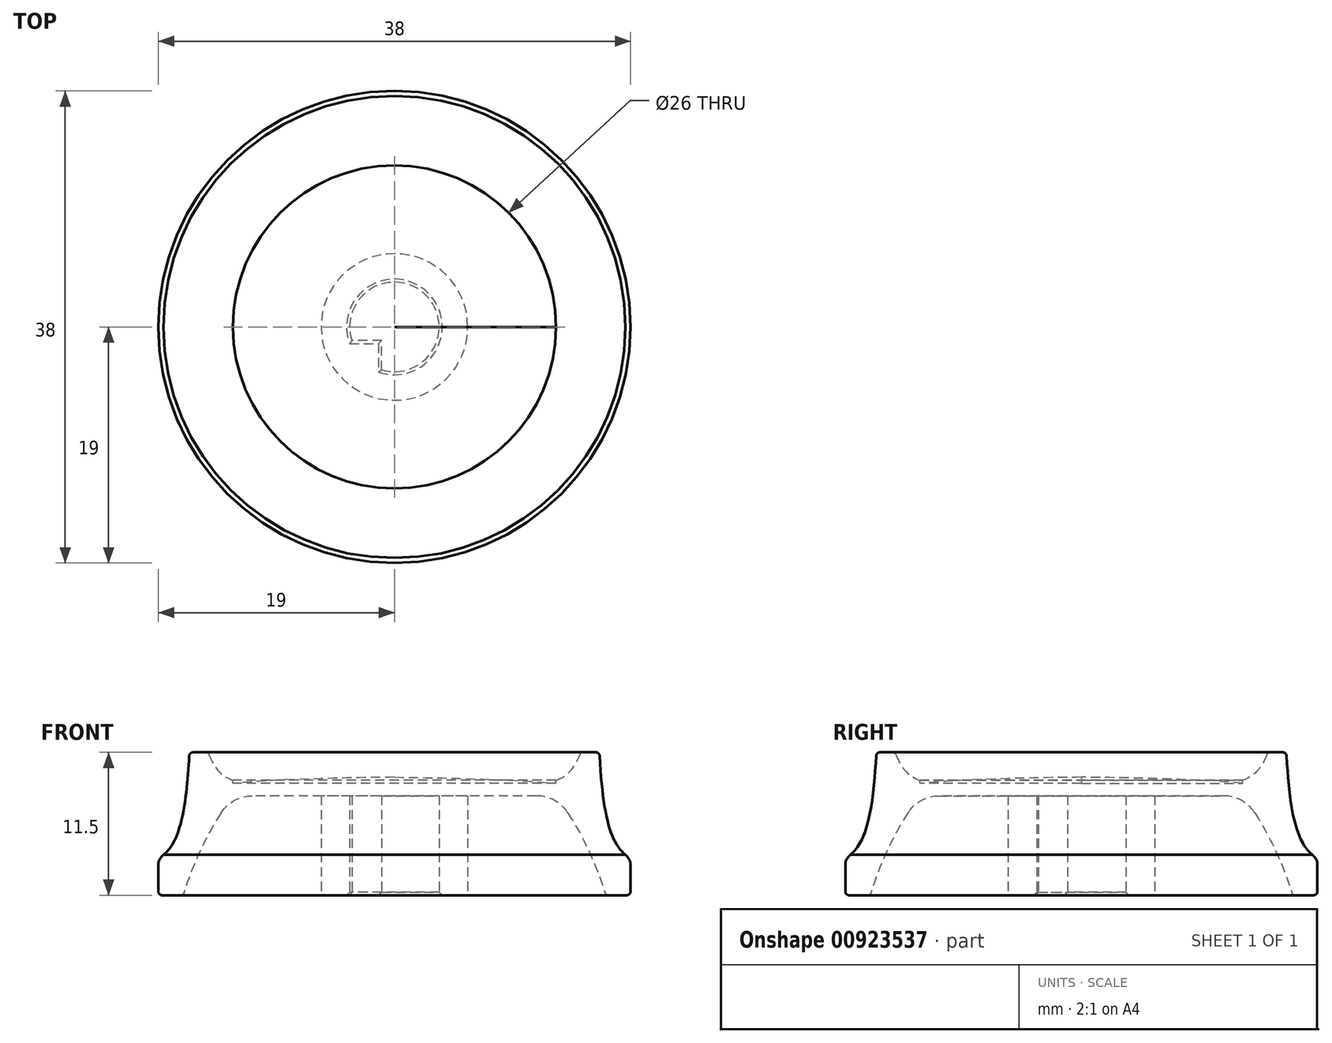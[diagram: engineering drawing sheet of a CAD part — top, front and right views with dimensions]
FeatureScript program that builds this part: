
annotation { "Feature Type Name" : "Feature", "Feature Type Description" : "" }
export const myFeature = defineFeature(function(context is Context, id is Id, definition is map)
    precondition{}
    {
        {
            var Q0;
            Q0=qCreatedBy(makeId("Top.planeOp"),FACE);
            var sketch = newSketch(context, id + "F0", { "sketchPlane" : qUnion([Q0])});
            skCircle(sketch, "E0", {"center": v(0, 0) * mm, "radius": 3.6 * mm});
            skLineSegment(sketch, "E1", {"start": v(0, -3.6) * mm, "end": v(0, -1.1) * mm});
            skLineSegment(sketch, "E2", {"start": v(0, -1.1) * mm, "end": v(3.43, -1.1) * mm});
            skLineSegment(sketch, "E3", {"start": v(3.43, -1.1) * mm, "end": v(1.03, -1.1) * mm});
            skLineSegment(sketch, "E4", {"start": v(1.03, -1.1) * mm, "end": v(1.03, -3.45) * mm});
            skLineSegment(sketch, "E5.MirrorCS", {"start": v(-1.03, -1.1) * mm, "end": v(-1.03, -3.45) * mm});
            skLineSegment(sketch, "E6.MirrorCS", {"start": v(0, -1.1) * mm, "end": v(-3.43, -1.1) * mm});
            skCircle(sketch, "E7.0", {"center": v(0, 0) * mm, "radius": 5.9 * mm});
            skCircle(sketch, "E8.0", {"center": v(0, 0) * mm, "radius": 5.1 * mm});
            skCircle(sketch, "E9.0", {"center": v(0, 0) * mm, "radius": 4.9 * mm});
            skSolve(sketch);
        }
        {
            var Q0;
            Q0 = qSketchRegion(id + "F0", true);
            var Q1;
            {var subQ0=sQuery(id+"F0.wireOp",EDGE,"E5.MirrorCS");Q1=makeQuery(id+"F0.imprint","IMPRINT",FACE,{"disambiguationData":[TD([[makeQuery(id+"F0.imprint","IMPRINT",EDGE,{"derivedFrom":subQ0}),-1.0]])]});}
            var Q2;
            {var subQ0=sQuery(id+"F0.wireOp",EDGE,"E3");Q2=makeQuery(id+"F0.imprint","IMPRINT",FACE,{"disambiguationData":[TD([[makeQuery(id+"F0.imprint","IMPRINT",EDGE,{"derivedFrom":subQ0}),1.0]])]});}
            var Q3;
            Q3=makeQuery(id+"F0.imprint","IMPRINT",FACE,{"disambiguationData":[TD([[makeQuery(id+"F0.imprint","IMPRINT",EDGE,{"derivedFrom":sQuery(id+"F0.wireOp",EDGE,"E9.0")}),1.0]])]});
            var Q4;
            Q4=makeQuery(id+"F0.imprint","IMPRINT",FACE,{"disambiguationData":[TD([[makeQuery(id+"F0.imprint","IMPRINT",EDGE,{"derivedFrom":sQuery(id+"F0.wireOp",EDGE,"E8.0")}),1.0]])]});
            extrude(context, id + "F1", {"entities" : qUnion([Q0, Q1, Q2, Q3, Q4]), "depth" : 8 * mm, "offsetDistance" : 25 * mm});
        }
        {
            var Q0;
            Q0=makeQuery(id+"F1.opExtrude","CAP_FACE",FACE,{"disambiguationData":[OSD([sQuery(id+"F0.wireOp",EDGE,"E0"),sQuery(id+"F0.wireOp",EDGE,"E3"),sQuery(id+"F0.wireOp",EDGE,"E4"),sQuery(id+"F0.wireOp",EDGE,"E5.MirrorCS"),sQuery(id+"F0.wireOp",EDGE,"E6.MirrorCS"),sQuery(id+"F0.wireOp",EDGE,"E7.0")])],"isStart":false});
            cPlane(context, id + "F2", {"entities" : qUnion([Q0]), "cplaneType" : CPlaneType.OFFSET, "offset" : 0 * mm, "width" : 150 * mm, "height" : 150 * mm});
        }
        {
            var Q0;
            Q0=qCreatedBy(id+"F2.planeOp",FACE);
            var sketch = newSketch(context, id + "F3", { "sketchPlane" : qUnion([Q0])});
            skCircle(sketch, "E10", {"center": v(0, 0) * mm, "radius": 5.9 * mm});
            skCircle(sketch, "E11.0", {"center": v(0, 0) * mm, "radius": 13 * mm});
            skSolve(sketch);
        }
        {
            var Q0;
            Q0 = qSketchRegion(id + "F3", true);
            var Q1;
            Q1=makeQuery(id+"F3.imprint","IMPRINT",FACE,{"disambiguationData":[TD([[makeQuery(id+"F3.imprint","IMPRINT",EDGE,{"derivedFrom":sQuery(id+"F3.wireOp",EDGE,"E10")}),1.0]])]});
            extrude(context, id + "F4", {"entities" : qUnion([Q0, Q1]), "operationType" : NewBodyOperationType.ADD, "depth" : 1.5 * mm, "offsetDistance" : 25 * mm});
        }
        {
            var Q0;
            Q0=qCreatedBy(makeId("Front.planeOp"),FACE);
            var sketch = newSketch(context, id + "F5", { "sketchPlane" : qUnion([Q0])});
            skLineSegment(sketch, "E12", {"start": v(0, 0) * mm, "end": v(0, 9.5) * mm});
            skLineSegment(sketch, "E13", {"start": v(0, 9.5) * mm, "end": v(13, 9.5) * mm});
            skLineSegment(sketch, "E14", {"start": v(13, 9.5) * mm, "end": v(13, 9) * mm});
            skFitSpline(sketch, "E15", {"points": [v(0, 9.5) * mm, v(13, 9) * mm], "startDerivative": vector(14.33, -0.14) * mm, "endDerivative": vector(7.51, -0.84) * mm});
            skLineSegment(sketch, "E16", {"start": v(13, 9.5) * mm, "end": v(13, 10.78) * mm});
            skLineSegment(sketch, "E17.top", {"start": v(0, 10.78) * mm, "end": v(13, 10.78) * mm});
            skLineSegment(sketch, "E17.left", {"start": v(0, 9.5) * mm, "end": v(0, 10.78) * mm});
            skSolve(sketch);
        }
        {
            var Q0;
            Q0 = qSketchRegion(id + "F5", true);
            var Q1;
            Q1=makeQuery(id+"F4.opExtrude","SWEPT_FACE",FACE,{"disambiguationData":[OSD([sQuery(id+"F3.wireOp",EDGE,"E11.0")])]});
            revolve(context, id + "F6", {"operationType" : NewBodyOperationType.REMOVE, "surfaceOperationType" : NewSurfaceOperationType.NEW, "entities" : qUnion([Q0]), "axis" : qUnion([Q1]), "revolveType" : RevolveType.FULL, "oppositeDirection" : true});
        }
        {
            var Q0;
            Q0=qCreatedBy(makeId("Front.planeOp"),FACE);
            var sketch = newSketch(context, id + "F7", { "sketchPlane" : qUnion([Q0])});
            skLineSegment(sketch, "E18", {"start": v(0, 0) * mm, "end": v(19, 0) * mm});
            skLineSegment(sketch, "E19", {"start": v(19, 0) * mm, "end": v(19, 2.5) * mm});
            skLineSegment(sketch, "E20", {"start": v(19, 2.5) * mm, "end": v(19, 11.5) * mm});
            skLineSegment(sketch, "E21", {"start": v(0, 0) * mm, "end": v(0, 8) * mm});
            skLineSegment(sketch, "E22", {"start": v(0, 8) * mm, "end": v(13, 8) * mm});
            skLineSegment(sketch, "E23", {"start": v(13, 8) * mm, "end": v(13, 11.5) * mm});
            skLineSegment(sketch, "E24", {"start": v(13, 11.5) * mm, "end": v(15, 11.5) * mm});
            skLineSegment(sketch, "E25", {"start": v(15, 11.5) * mm, "end": v(16.5, 11.5) * mm});
            skLineSegment(sketch, "E26", {"start": v(19, 2.5) * mm, "end": v(18.6, 2.5) * mm});
            skLineSegment(sketch, "E27", {"start": v(18.6, 2.5) * mm, "end": v(18.6, 3.25) * mm});
            skFitSpline(sketch, "E28", {"points": [v(16.5, 11.5) * mm, v(18.6, 3.25) * mm], "startDerivative": vector(0.75, -14.7) * mm, "endDerivative": vector(3.82, -3.03) * mm});
            skFitSpline(sketch, "E29", {"points": [v(18.6, 3.25) * mm, v(19, 2.5) * mm], "startDerivative": vector(0.5, -0.48) * mm, "endDerivative": vector(0, -0.96) * mm});
            skLineSegment(sketch, "E30", {"start": v(13, 8) * mm, "end": v(13, 9) * mm});
            skLineSegment(sketch, "E31", {"start": v(13, 9) * mm, "end": v(13, 9.25) * mm});
            skFitSpline(sketch, "E32", {"points": [v(13, 9.25) * mm, v(15, 11.5) * mm], "startDerivative": vector(3.03, 1.17) * mm, "endDerivative": vector(1.49, 3.83) * mm});
            skLineSegment(sketch, "E33", {"start": v(19, 0) * mm, "end": v(17, 0) * mm});
            skFitSpline(sketch, "E34", {"points": [v(13, 8) * mm, v(17, 0) * mm], "startDerivative": vector(5.15, -6.81) * mm, "endDerivative": vector(2.57, -8.62) * mm});
            skSolve(sketch);
        }
        {
            var Q0;
            Q0=makeQuery(id+"F7.imprint","IMPRINT",FACE,{"disambiguationData":[TD([[makeQuery(id+"F7.imprint","IMPRINT",EDGE,{"derivedFrom":sQuery(id+"F7.wireOp",EDGE,"E26")}),-1.0]])]});
            var Q1;
            Q1=makeQuery(id+"F7.imprint","IMPRINT",FACE,{"disambiguationData":[TD([[makeQuery(id+"F7.imprint","IMPRINT",EDGE,{"derivedFrom":sQuery(id+"F7.wireOp",EDGE,"E19")}),1.0]])]});
            var Q2;
            Q2=makeQuery(id+"F4.opExtrude","SWEPT_FACE",FACE,{"disambiguationData":[OSD([sQuery(id+"F3.wireOp",EDGE,"E11.0")])]});
            revolve(context, id + "F8", {"operationType" : NewBodyOperationType.ADD, "surfaceOperationType" : NewSurfaceOperationType.NEW, "entities" : qUnion([Q0, Q1]), "axis" : qUnion([Q2]), "revolveType" : RevolveType.FULL});
        }
        {
            var Q0;
            Q0=makeQuery(id+"F8.opRevolve","SWEPT_EDGE",EDGE,{"disambiguationData":[OSD([sQuery(id+"F7.wireOp",EDGE,"E25"),sQuery(id+"F7.wireOp",EDGE,"E28")])]});
            var Q1;
            Q1=makeQuery(id+"F8.opRevolve","SWEPT_EDGE",EDGE,{"disambiguationData":[OSD([sQuery(id+"F7.wireOp",EDGE,"E24"),sQuery(id+"F7.wireOp",EDGE,"E25"),sQuery(id+"F7.wireOp",EDGE,"E32")])]});
            var Q2;
            Q2=makeQuery(id+"F8.opRevolve","SWEPT_EDGE",EDGE,{"disambiguationData":[OSD([sQuery(id+"F7.wireOp",EDGE,"E19"),sQuery(id+"F7.wireOp",EDGE,"E33")])]});
            var Q3;
            Q3=makeQuery(id+"F8.opRevolve","SWEPT_EDGE",EDGE,{"disambiguationData":[OSD([sQuery(id+"F7.wireOp",EDGE,"E18"),sQuery(id+"F7.wireOp",EDGE,"E33"),sQuery(id+"F7.wireOp",EDGE,"E34")])]});
            fillet(context, id + "F9", {"entities" : qUnion([Q0, Q1, Q2, Q3]), "radius" : .3 * mm, "tangentPropagation" : true, "allowEdgeOverflow" : false});
        }
        {
            var Q0;
            Q0=makeQuery(id+"F1.opExtrude","CAP_EDGE",EDGE,{"disambiguationData":[OSD([sQuery(id+"F0.wireOp",EDGE,"E7.0")])],"isStart":false});
            var Q1;
            Q1=makeQuery(id+"F8.boolean.opBoolean","MERGE",EDGE,{"derivedFrom":[makeQuery(id+"F4.opExtrude","CAP_EDGE",EDGE,{"disambiguationData":[OSD([sQuery(id+"F3.wireOp",EDGE,"E11.0")])],"isStart":true}),makeQuery(id+"F8.opRevolve","SWEPT_EDGE",EDGE,{"disambiguationData":[OSD([sQuery(id+"F7.wireOp",EDGE,"E22"),sQuery(id+"F7.wireOp",EDGE,"E30"),sQuery(id+"F7.wireOp",EDGE,"E34")])]})]});
            fillet(context, id + "F10", {"entities" : qUnion([Q0, Q1]), "radius" : 3 * mm, "tangentPropagation" : true, "allowEdgeOverflow" : false});
        }
        {
            var Q0;
            Q0=makeQuery(id+"F1.opExtrude","CAP_EDGE",EDGE,{"disambiguationData":[OSD([sQuery(id+"F0.wireOp",EDGE,"E6.MirrorCS")])],"isStart":true});
            var Q1;
            Q1=makeQuery(id+"F1.opExtrude","CAP_EDGE",EDGE,{"disambiguationData":[OSD([sQuery(id+"F0.wireOp",EDGE,"E5.MirrorCS")])],"isStart":true});
            var Q2;
            Q2=makeQuery(id+"F1.opExtrude","CAP_EDGE",EDGE,{"disambiguationData":[OSD([sQuery(id+"F0.wireOp",EDGE,"E4")])],"isStart":true});
            var Q3;
            Q3=makeQuery(id+"F1.opExtrude","CAP_EDGE",EDGE,{"disambiguationData":[OSD([sQuery(id+"F0.wireOp",EDGE,"E3")])],"isStart":true});
            var Q4;
            {var subQ0=sQuery(id+"F0.wireOp",EDGE,"E0");var subQ1=makeQuery(id+"F0.imprint","INTERSECT",VERTEX,{"derivedFrom":[subQ0,sQuery(id+"F0.wireOp",EDGE,"E1")]});Q4=makeQuery(id+"F1.opExtrude","CAP_EDGE",EDGE,{"disambiguationData":[OSD([subQ0]),TDD([makeQuery(id+"F0.imprint","IMPRINT",EDGE,{"disambiguationData":[TD([[subQ1,1.0]])],"derivedFrom":subQ0}),makeQuery(id+"F0.imprint","IMPRINT",EDGE,{"disambiguationData":[TD([[subQ1,-1.0]])],"derivedFrom":subQ0})])],"isStart":true});}
            var Q5;
            {var subQ0=sQuery(id+"F0.wireOp",EDGE,"E0");Q5=makeQuery(id+"F1.opExtrude","CAP_EDGE",EDGE,{"disambiguationData":[OSD([subQ0]),TDD([makeQuery(id+"F0.imprint","IMPRINT",EDGE,{"disambiguationData":[TD([[makeQuery(id+"F0.imprint","INTERSECT",VERTEX,{"derivedFrom":[subQ0,sQuery(id+"F0.wireOp",EDGE,"E3")]}),-1.0]])],"derivedFrom":subQ0})])],"isStart":true});}
            var Q6;
            Q6=makeQuery(id+"F5ZplvMa2vL8Z5Y_1.boolean.opBoolean","COPY",EDGE,{"derivedFrom":makeQuery(id+"F5ZplvMa2vL8Z5Y_1.opExtrude","CAP_EDGE",EDGE,{"disambiguationData":[OSD([sQuery(id+"F0.wireOp",EDGE,"E8.0")])],"isStart":true})});
            var Q7;
            Q7=makeQuery(id+"F5ZplvMa2vL8Z5Y_1.boolean.opBoolean","COPY",EDGE,{"derivedFrom":makeQuery(id+"F5ZplvMa2vL8Z5Y_1.opExtrude","CAP_EDGE",EDGE,{"disambiguationData":[OSD([sQuery(id+"F0.wireOp",EDGE,"E9.0")])],"isStart":true})});
            chamfer(context, id + "F11", {"entities" : qUnion([Q0, Q1, Q2, Q3, Q4, Q5, Q6, Q7]), "width" : .25 * mm, "tangentPropagation" : true});
        }
    });
